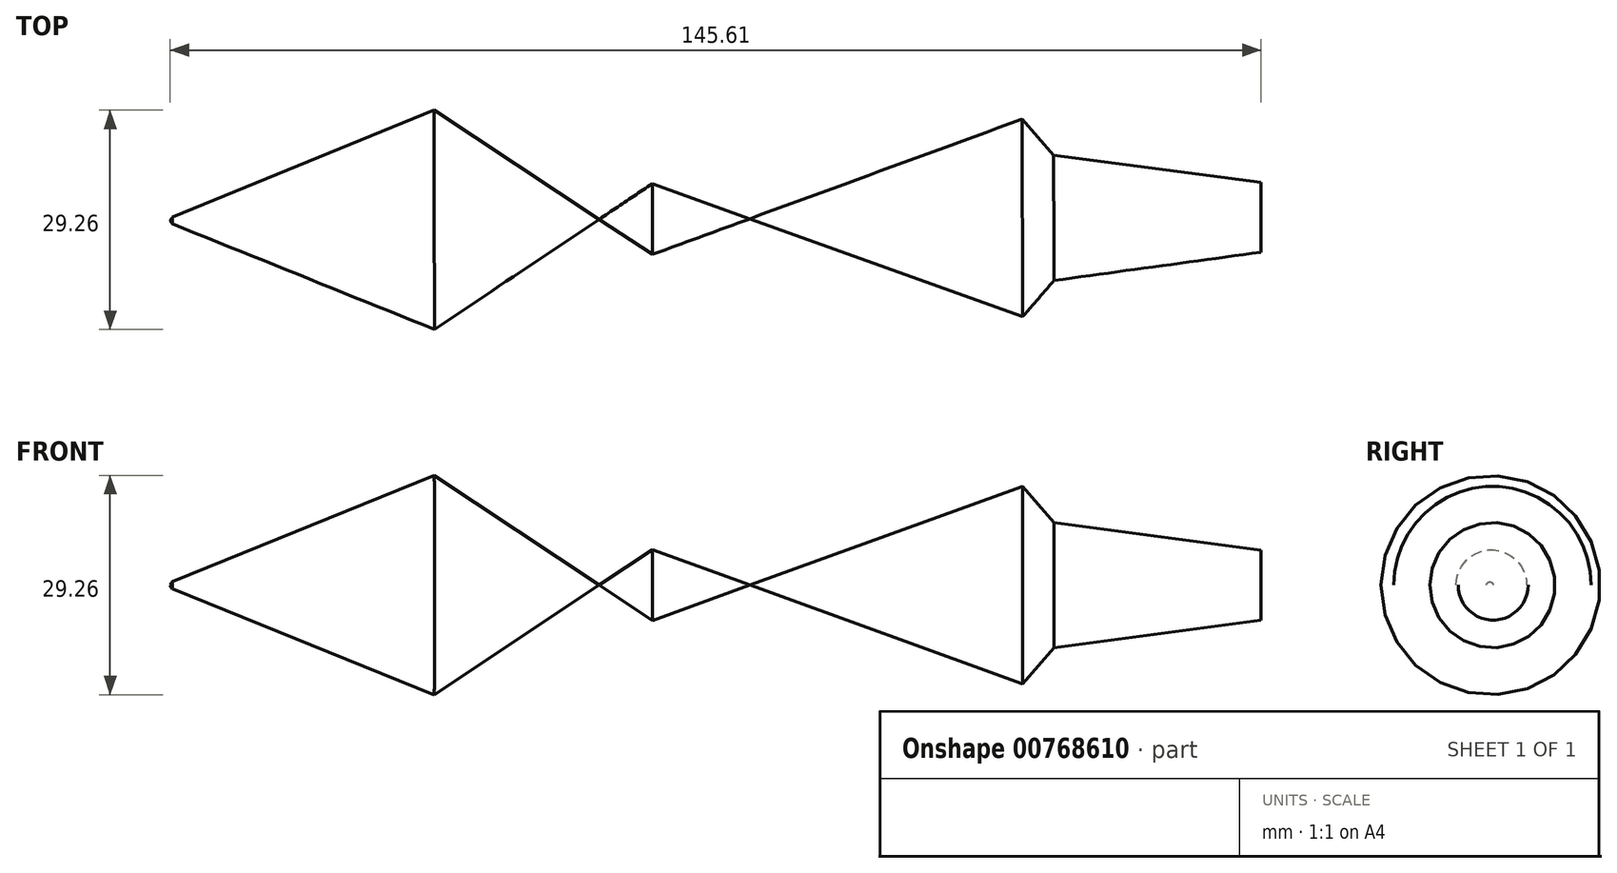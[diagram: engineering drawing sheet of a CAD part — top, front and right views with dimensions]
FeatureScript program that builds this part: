
annotation { "Feature Type Name" : "Feature", "Feature Type Description" : "" }
export const myFeature = defineFeature(function(context is Context, id is Id, definition is map)
    precondition{}
    {
        {
            var Q0;
            Q0=qCreatedBy(makeId("Top.planeOp"),FACE);
            var sketch = newSketch(context, id + "F0", { "sketchPlane" : qUnion([Q0])});
            skLineSegment(sketch, "E0", {"start": v(-75.95, 0) * mm, "end": v(-41.06, 14.29) * mm});
            skLineSegment(sketch, "E1", {"start": v(-41.06, 14.29) * mm, "end": v(-11.88, -4.96) * mm});
            skLineSegment(sketch, "E2", {"start": v(-11.88, -4.96) * mm, "end": v(37.45, 13.08) * mm});
            skLineSegment(sketch, "E3", {"start": v(37.45, 13.08) * mm, "end": v(41.66, 8.27) * mm});
            skLineSegment(sketch, "E4", {"start": v(41.66, 8.27) * mm, "end": v(69.33, 4.66) * mm});
            skLineSegment(sketch, "E5", {"start": v(69.33, 4.66) * mm, "end": v(69.33, 0) * mm});
            skLineSegment(sketch, "E6", {"start": v(-76.25, -0.45) * mm, "end": v(69.33, 0) * mm});
            skLineSegment(sketch, "E7", {"start": v(-76.25, -0.45) * mm, "end": v(-75.95, 0) * mm});
            skSolve(sketch);
        }
        {
            var Q0;
            {var subQ0=sQuery(id+"F0.wireOp",EDGE,"E0");Q0=makeQuery(id+"F0.imprint","IMPRINT",FACE,{"disambiguationData":[TD([[makeQuery(id+"F0.imprint","IMPRINT",EDGE,{"derivedFrom":subQ0}),-1.0]])]});}
            var Q1;
            {var subQ0=sQuery(id+"F0.wireOp",EDGE,"E2");var subQ1=sQuery(id+"F0.wireOp",EDGE,"E1");var subQ2=makeQuery(id+"F0.imprint","INTERSECT",VERTEX,{"derivedFrom":[subQ1,subQ0]});Q1=makeQuery(id+"F0.imprint","IMPRINT",FACE,{"disambiguationData":[TD([[makeQuery(id+"F0.imprint","IMPRINT",EDGE,{"disambiguationData":[TD([[subQ2,1.0]])],"derivedFrom":subQ1}),1.0]])]});}
            var Q2;
            {var subQ1=sQuery(id+"F0.wireOp",EDGE,"E3");Q2=makeQuery(id+"F0.imprint","IMPRINT",FACE,{"disambiguationData":[TD([[makeQuery(id+"F0.imprint","IMPRINT",EDGE,{"derivedFrom":subQ1}),-1.0]])]});}
            var Q3;
            Q3=sQuery(id+"F0.wireOp",EDGE,"E6");
            revolve(context, id + "F1", {"surfaceOperationType" : NewSurfaceOperationType.NEW, "entities" : qUnion([Q0, Q1, Q2]), "axis" : qUnion([Q3]), "revolveType" : RevolveType.FULL});
        }
    });
